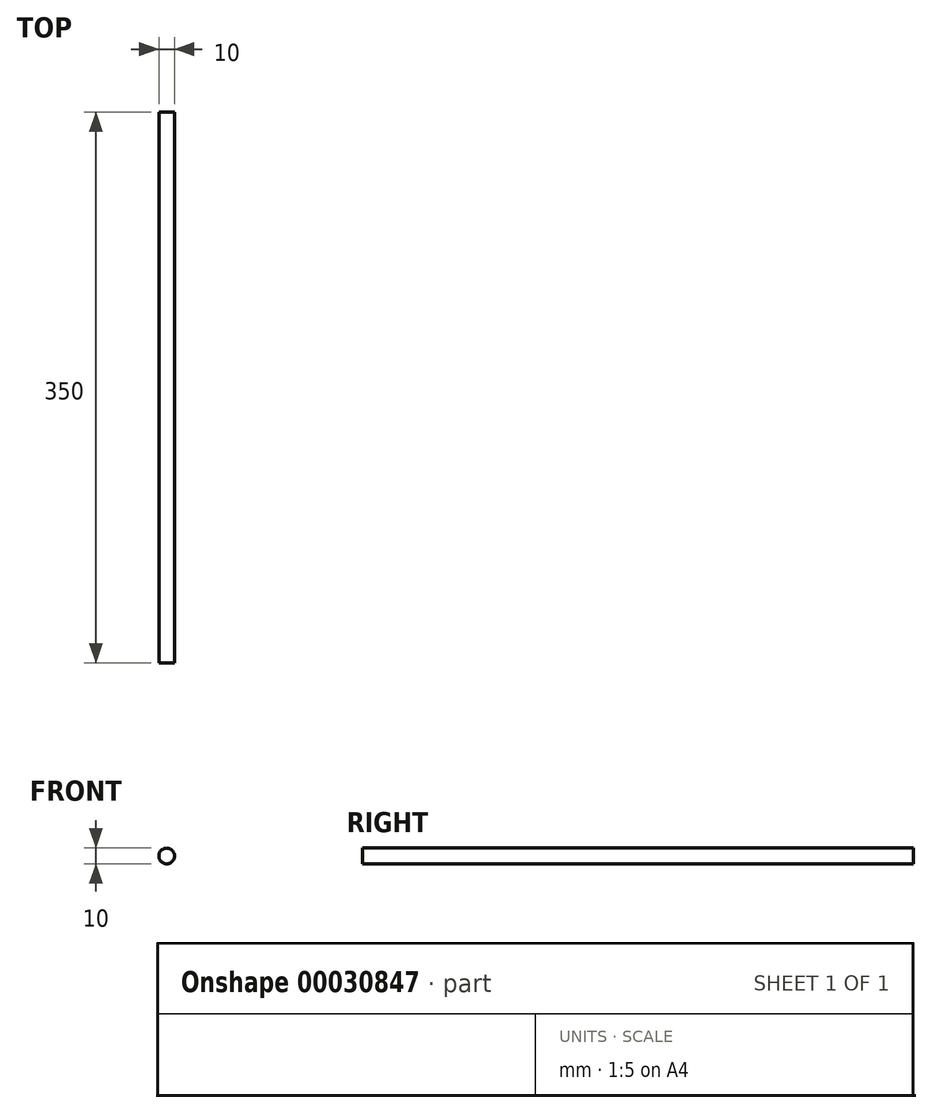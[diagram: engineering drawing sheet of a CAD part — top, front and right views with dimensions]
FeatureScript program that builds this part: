
annotation { "Feature Type Name" : "Feature", "Feature Type Description" : "" }
export const myFeature = defineFeature(function(context is Context, id is Id, definition is map)
    precondition{}
    {
        {
            var Q0;
            Q0=qCreatedBy(makeId("Top.planeOp"),FACE);
            var sketch = newSketch(context, id + "F0", { "sketchPlane" : qUnion([Q0])});
            skLineSegment(sketch, "E0", {"start": v(0, 0) * mm, "end": v(0, 350) * mm});
            skSolve(sketch);
        }
        {
            var Q0;
            Q0=qCreatedBy(makeId("Front.planeOp"),FACE);
            var sketch = newSketch(context, id + "F1", { "sketchPlane" : qUnion([Q0])});
            skCircle(sketch, "E1", {"center": v(0, 0) * mm, "radius": 5 * mm});
            skSolve(sketch);
        }
        {
            var Q0;
            Q0=makeQuery(id+"F1.imprint","IMPRINT",FACE,{"disambiguationData":[TD([[makeQuery(id+"F1.imprint","IMPRINT",EDGE,{"derivedFrom":sQuery(id+"F1.wireOp",EDGE,"E1")}),1.0]])]});
            var Q1;
            Q1=sQuery(id+"F0.wireOp",EDGE,"E0");
            sweep(context, id + "F2", {"profiles" : qUnion([Q0]), "path" : qUnion([Q1])});
        }
    });
